# Revit family: Faucet-Single_Handle-American Standard-Delancey-7052121_Series
name_source: partatom
category: Plumbing Fixtures
units: mm (PartAtom-declared; Revit-internal decimal feet)

## family parameters
Always vertical = Yes
Cut with Voids When Loaded = No
OmniClass Number = 23.45.55.14
OmniClass Title = Single Faucets
Part Type = Normal
Room Calculation Point = No
Round Connector Dimension = Use Diameter
Shared = No
Work Plane-Based = Yes

## types (4) — shared parameters
ADA Compliant = Yes
Assembly Code = D2020300
Brass Push Pop-up Drain = Yes
CEC Compliant = Yes
CW Connection = No
CWFU = 1.5
CalGreen Compliant = Yes
Compliance Certifications = ANSI A117.1, ASME A112.18.1, CSA B125.1, NSF 61/Section 9, NSF 372
Deck Plate = No
Default Elevation = 0"
Description = Delancey® Single Hole Single-Handle Bathroom Faucet 1.2 gpm/4.5 L/min With Lever Handle
Drain Location Height = 14 3/16"
Drain Location Length = 10 5/16"
Flow Rate = 1.2 gpm/4.5 L/min maximum flow rate
HW Connection = No
HWFU = 1.5
Height = 8"
Installation Instruction Link = https://lixil.cdn.celum.cloud
Installation Type = Deck-Mounted
Length = 5"
Manufacturer = American Standard
Mounting Deck Height = 0"
Product Documentation Link = https://lixil.cdn.celum.cloud
Product Page URL = https://www.americanstandard-us.com
Spout Height = 5 1/4"
Tempered Water Connection = Yes
Tempered Water Connection Diameter = 3/8"
URL = https://www.americanstandard-us.com
Vent Connection = No
WFU = 2
Warranty Information = Limited Lifetime Warranty
Waste Connection = Yes

## per-type parameters (varying)
| type | Finish | Material |
| 7052121.002 | Brass-American Standard-002-Polished Chrome | Brass-American Standard-002-Polished Chrome |
| 7052121.295 | Brass-American Standard-295-Brushed Nickel | Brass-American Standard-295-Brushed Nickel |
| 7052121.013 | Brass-American Standard-013-Polished Nickel | Brass-American Standard-013-Polished Nickel |
| 7052121.278 | Brass-American Standard-278-Legacy Bronze | Brass-American Standard-278-Legacy Bronze |

note: column(s) folded — value = type name in every type: Model

## geometry (parser evidence)
native form markers: Sweep x4
no freeform markers — native parametric forms only
